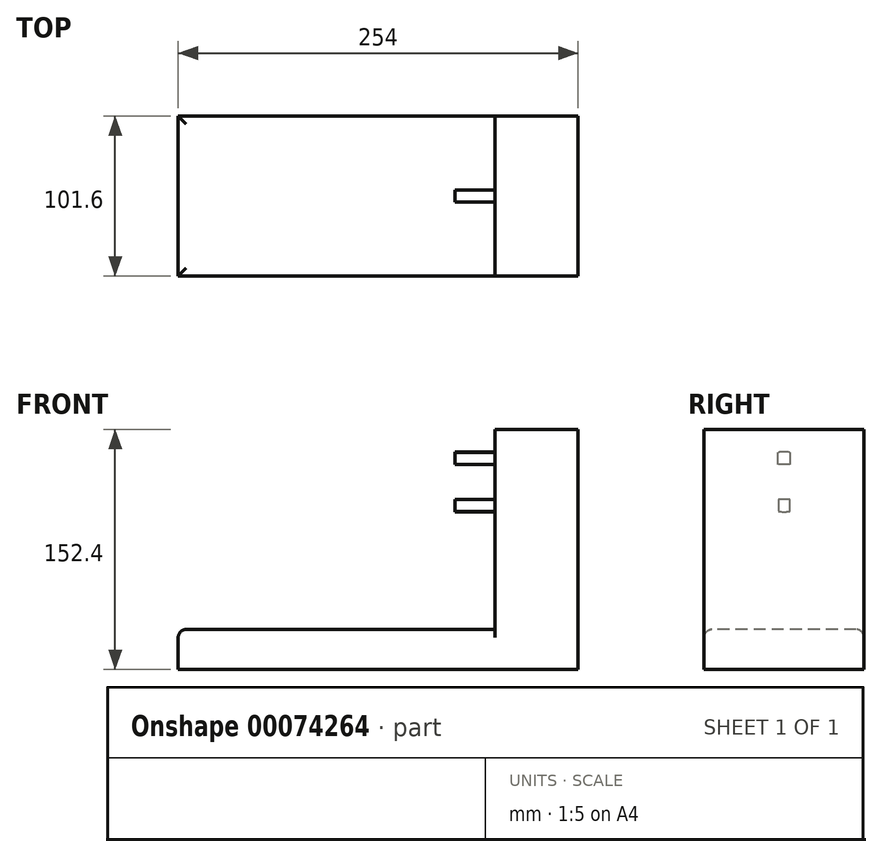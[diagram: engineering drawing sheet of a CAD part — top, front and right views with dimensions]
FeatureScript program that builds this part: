
annotation { "Feature Type Name" : "Feature", "Feature Type Description" : "" }
export const myFeature = defineFeature(function(context is Context, id is Id, definition is map)
    precondition{}
    {
        {
            var Q0;
            Q0=qCreatedBy(makeId("Top.planeOp"),FACE);
            var sketch = newSketch(context, id + "F0", { "sketchPlane" : qUnion([Q0])});
            skLineSegment(sketch, "E0.bottom", {"start": v(-121.5, 23.45) * mm, "end": v(132.5, 23.45) * mm});
            skLineSegment(sketch, "E0.top", {"start": v(-121.5, -78.15) * mm, "end": v(132.5, -78.15) * mm});
            skLineSegment(sketch, "E0.left", {"start": v(-121.5, 23.45) * mm, "end": v(-121.5, -78.15) * mm});
            skLineSegment(sketch, "E0.right", {"start": v(132.5, 23.45) * mm, "end": v(132.5, -78.15) * mm});
            skSolve(sketch);
        }
        {
            var Q0;
            Q0=makeQuery(id+"F0.imprint","IMPRINT",FACE,{"disambiguationData":[TD([[makeQuery(id+"F0.imprint","IMPRINT",EDGE,{"derivedFrom":sQuery(id+"F0.wireOp",EDGE,"E0.bottom")}),-1.0]])]});
            extrude(context, id + "F1", {"entities" : qUnion([Q0]), "depth" : 25.4 * mm});
        }
        {
            var Q0;
            Q0=makeQuery(id+"F1.opExtrude","CAP_FACE",FACE,{"disambiguationData":[OSD([sQuery(id+"F0.wireOp",EDGE,"E0.bottom"),sQuery(id+"F0.wireOp",EDGE,"E0.top"),sQuery(id+"F0.wireOp",EDGE,"E0.left"),sQuery(id+"F0.wireOp",EDGE,"E0.right")])],"isStart":false});
            var sketch = newSketch(context, id + "F2", { "sketchPlane" : qUnion([Q0])});
            skLineSegment(sketch, "E1.bottom", {"start": v(79.76, 23.45) * mm, "end": v(132.5, 23.45) * mm});
            skLineSegment(sketch, "E1.top", {"start": v(79.76, -78.15) * mm, "end": v(132.5, -78.15) * mm});
            skLineSegment(sketch, "E1.left", {"start": v(79.76, 23.45) * mm, "end": v(79.76, -78.15) * mm});
            skLineSegment(sketch, "E1.right", {"start": v(132.5, 23.45) * mm, "end": v(132.5, -78.15) * mm});
            skSolve(sketch);
        }
        {
            var Q0;
            Q0=makeQuery(id+"F2.imprint","IMPRINT",FACE,{"disambiguationData":[TD([[makeQuery(id+"F2.imprint","IMPRINT",EDGE,{"derivedFrom":sQuery(id+"F2.wireOp",EDGE,"E1.bottom")}),-1.0]])]});
            extrude(context, id + "F3", {"entities" : qUnion([Q0]), "operationType" : NewBodyOperationType.ADD, "depth" : 127 * mm});
        }
        {
            var Q0;
            Q0=makeQuery(id+"F3.opExtrude","SWEPT_FACE",FACE,{"disambiguationData":[OSD([sQuery(id+"F2.wireOp",EDGE,"E1.left")])]});
            var sketch = newSketch(context, id + "F4", { "sketchPlane" : qUnion([Q0])});
            skCircle(sketch, "E2", {"center": v(27.35, 119.15) * mm, "radius": 19.05 * mm, "construction": true});
            skPoint(sketch, "E2.centerSnap0", {"position": v(27.35, 152.4) * mm});
            skLineSegment(sketch, "E3", {"start": v(23.54, 137.82) * mm, "end": v(23.54, 130.2) * mm});
            skLineSegment(sketch, "E4", {"start": v(23.54, 130.2) * mm, "end": v(31.16, 130.2) * mm});
            skLineSegment(sketch, "E5", {"start": v(31.16, 130.2) * mm, "end": v(31.16, 137.82) * mm});
            skLineSegment(sketch, "E6", {"start": v(23.64, 100.47) * mm, "end": v(23.64, 108.09) * mm});
            skLineSegment(sketch, "E7", {"start": v(23.64, 108.09) * mm, "end": v(31.05, 108.09) * mm});
            skLineSegment(sketch, "E8", {"start": v(31.05, 108.09) * mm, "end": v(31.05, 100.47) * mm});
            skLineSegment(sketch, "E9", {"start": v(27.35, 100.1) * mm, "end": v(27.35, 138.2) * mm, "construction": true});
            skPoint(sketch, "E10", {"position": v(27.35, 130.2) * mm});
            skPoint(sketch, "E11", {"position": v(27.35, 108.09) * mm});
            skCircle(sketch, "E12", {"center": v(27.35, 119.15) * mm, "radius": 19.05 * mm});
            skSolve(sketch);
        }
        {
            var Q0;
            {var subQ0=sQuery(id+"F4.wireOp",EDGE,"E3");Q0=makeQuery(id+"F4.imprint","IMPRINT",FACE,{"disambiguationData":[TD([[makeQuery(id+"F4.imprint","IMPRINT",EDGE,{"derivedFrom":subQ0}),1.0]])]});}
            var Q1;
            {var subQ0=sQuery(id+"F4.wireOp",EDGE,"E6");Q1=makeQuery(id+"F4.imprint","IMPRINT",FACE,{"disambiguationData":[TD([[makeQuery(id+"F4.imprint","IMPRINT",EDGE,{"derivedFrom":subQ0}),-1.0]])]});}
            extrude(context, id + "F5", {"entities" : qUnion([Q0, Q1]), "operationType" : NewBodyOperationType.ADD, "depth" : 25.4 * mm});
        }
        {
            var Q0;
            Q0=makeQuery(id+"F1.opExtrude","CAP_EDGE",EDGE,{"disambiguationData":[OSD([sQuery(id+"F0.wireOp",EDGE,"E0.top")])],"isStart":false});
            var Q1;
            Q1=makeQuery(id+"F1.opExtrude","CAP_EDGE",EDGE,{"disambiguationData":[OSD([sQuery(id+"F0.wireOp",EDGE,"E0.left")])],"isStart":false});
            var Q2;
            Q2=makeQuery(id+"F1.opExtrude","CAP_EDGE",EDGE,{"disambiguationData":[OSD([sQuery(id+"F0.wireOp",EDGE,"E0.bottom")])],"isStart":false});
            fillet(context, id + "F6", {"entities" : qUnion([Q0, Q1, Q2]), "radius" : 5.08 * mm, "tangentPropagation" : true, "allowEdgeOverflow" : false});
        }
    });
